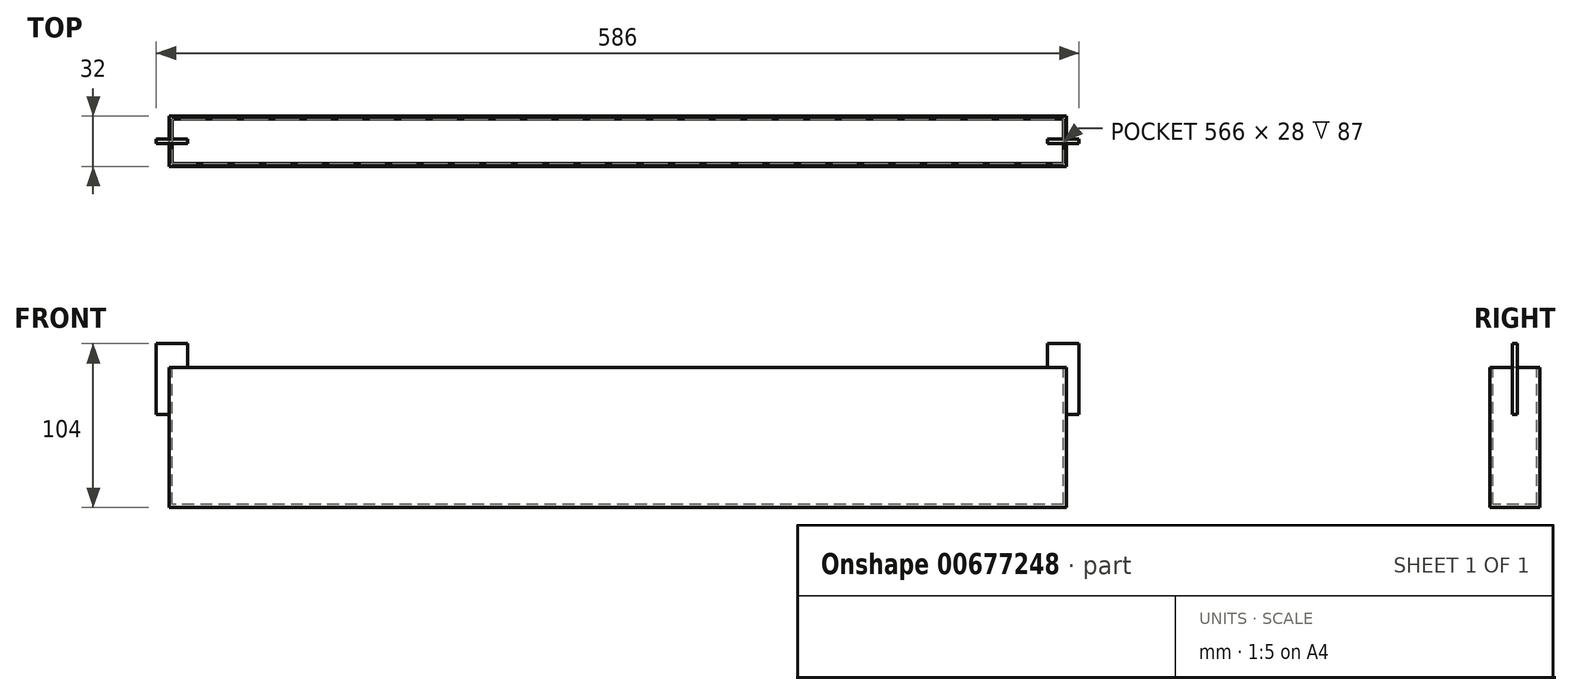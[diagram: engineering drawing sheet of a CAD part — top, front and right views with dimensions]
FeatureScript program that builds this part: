
annotation { "Feature Type Name" : "Feature", "Feature Type Description" : "" }
export const myFeature = defineFeature(function(context is Context, id is Id, definition is map)
    precondition{}
    {
        {
            var Q0;
            Q0=qCreatedBy(makeId("Top.planeOp"),FACE);
            var sketch = newSketch(context, id + "F0", { "sketchPlane" : qUnion([Q0])});
            skLineSegment(sketch, "E0.bottom", {"start": v(285, 16) * mm, "end": v(-285, 16) * mm});
            skLineSegment(sketch, "E0.top", {"start": v(285, -16) * mm, "end": v(-285, -16) * mm});
            skLineSegment(sketch, "E0.left", {"start": v(285, 16) * mm, "end": v(285, -16) * mm});
            skLineSegment(sketch, "E0.right", {"start": v(-285, 16) * mm, "end": v(-285, -16) * mm});
            skPoint(sketch, "E0.middle", {"position": v(0, 0) * mm});
            skSolve(sketch);
        }
        {
            var Q0;
            Q0=makeQuery(id+"F0.imprint","IMPRINT",FACE,{"disambiguationData":[TD([[makeQuery(id+"F0.imprint","IMPRINT",EDGE,{"derivedFrom":sQuery(id+"F0.wireOp",EDGE,"E0.bottom")}),1.0]])]});
            extrude(context, id + "F1", {"entities" : qUnion([Q0]), "depth" : 89 * mm, "offsetDistance" : 25 * mm});
        }
        {
            var Q0;
            Q0=makeQuery(id+"F1.opExtrude","SWEPT_FACE",FACE,{"disambiguationData":[OSD([sQuery(id+"F0.wireOp",EDGE,"E0.right")])]});
            var sketch = newSketch(context, id + "F2", { "sketchPlane" : qUnion([Q0])});
            skLineSegment(sketch, "E1.bottom", {"start": v(1.5, 89) * mm, "end": v(-1.5, 89) * mm});
            skLineSegment(sketch, "E1.top", {"start": v(1.5, 59) * mm, "end": v(-1.5, 59) * mm});
            skLineSegment(sketch, "E1.left", {"start": v(1.5, 89) * mm, "end": v(1.5, 59) * mm});
            skLineSegment(sketch, "E1.right", {"start": v(-1.5, 89) * mm, "end": v(-1.5, 59) * mm});
            skPoint(sketch, "E1.middle", {"position": v(0, 74) * mm});
            skSolve(sketch);
        }
        {
            var Q0;
            Q0=makeQuery(id+"F2.imprint","IMPRINT",FACE,{"disambiguationData":[TD([[makeQuery(id+"F2.imprint","IMPRINT",EDGE,{"derivedFrom":sQuery(id+"F2.wireOp",EDGE,"E1.bottom")}),-1.0]])]});
            extrude(context, id + "F3", {"entities" : qUnion([Q0]), "operationType" : NewBodyOperationType.ADD, "depth" : 8 * mm, "offsetDistance" : 25 * mm});
        }
        {
            var Q0;
            Q0=makeQuery(id+"F3.boolean.opBoolean","MERGE",FACE,{"derivedFrom":[makeQuery(id+"F1.opExtrude","CAP_FACE",FACE,{"disambiguationData":[OSD([sQuery(id+"F0.wireOp",EDGE,"E0.bottom"),sQuery(id+"F0.wireOp",EDGE,"E0.top"),sQuery(id+"F0.wireOp",EDGE,"E0.left"),sQuery(id+"F0.wireOp",EDGE,"E0.right")])],"isStart":false}),makeQuery(id+"F3.opExtrude","SWEPT_FACE",FACE,{"disambiguationData":[OSD([sQuery(id+"F2.wireOp",EDGE,"E1.bottom")])]})]});
            var sketch = newSketch(context, id + "F4", { "sketchPlane" : qUnion([Q0])});
            skLineSegment(sketch, "E2.bottom", {"start": v(-293, 1.5) * mm, "end": v(-285, 1.5) * mm});
            skLineSegment(sketch, "E2.top", {"start": v(-293, -1.5) * mm, "end": v(-285, -1.5) * mm});
            skLineSegment(sketch, "E2.left", {"start": v(-293, 1.5) * mm, "end": v(-293, -1.5) * mm});
            skLineSegment(sketch, "E2.right", {"start": v(-285, 1.5) * mm, "end": v(-285, -1.5) * mm});
            skSolve(sketch);
        }
        {
            var Q0;
            Q0=makeQuery(id+"F4.imprint","IMPRINT",FACE,{"disambiguationData":[TD([[makeQuery(id+"F4.imprint","IMPRINT",EDGE,{"derivedFrom":sQuery(id+"F4.wireOp",EDGE,"E2.bottom")}),-1.0]])]});
            extrude(context, id + "F5", {"entities" : qUnion([Q0]), "operationType" : NewBodyOperationType.ADD, "depth" : 15 * mm, "offsetDistance" : 25 * mm});
        }
        {
            var Q0;
            Q0=makeQuery(id+"F3.boolean.opBoolean","MERGE",FACE,{"derivedFrom":[makeQuery(id+"F1.opExtrude","CAP_FACE",FACE,{"disambiguationData":[OSD([sQuery(id+"F0.wireOp",EDGE,"E0.bottom"),sQuery(id+"F0.wireOp",EDGE,"E0.top"),sQuery(id+"F0.wireOp",EDGE,"E0.left"),sQuery(id+"F0.wireOp",EDGE,"E0.right")])],"isStart":false}),makeQuery(id+"F3.opExtrude","SWEPT_FACE",FACE,{"disambiguationData":[OSD([sQuery(id+"F2.wireOp",EDGE,"E1.bottom")])]})]});
            var sketch = newSketch(context, id + "F6", { "sketchPlane" : qUnion([Q0])});
            skLineSegment(sketch, "E3.bottom", {"start": v(283, 14) * mm, "end": v(-283, 14) * mm});
            skLineSegment(sketch, "E3.top", {"start": v(283, -14) * mm, "end": v(-283, -14) * mm});
            skLineSegment(sketch, "E3.left", {"start": v(283, 14) * mm, "end": v(283, -14) * mm});
            skLineSegment(sketch, "E3.right", {"start": v(-283, 14) * mm, "end": v(-283, -14) * mm});
            skPoint(sketch, "E3.middle", {"position": v(0, 0) * mm});
            skSolve(sketch);
        }
        {
            var Q0;
            {var subQ1=sQuery(id+"F6.wireOp",EDGE,"E3.bottom");Q0=makeQuery(id+"F6.imprint","IMPRINT",FACE,{"disambiguationData":[TD([[makeQuery(id+"F6.imprint","IMPRINT",EDGE,{"derivedFrom":subQ1}),1.0]])]});}
            extrude(context, id + "F7", {"entities" : qUnion([Q0]), "operationType" : NewBodyOperationType.REMOVE, "oppositeDirection" : true, "depth" : 87 * mm, "offsetDistance" : 25 * mm});
        }
        {
            var Q0;
            Q0=makeQuery(id+"F5.opExtrude","SWEPT_FACE",FACE,{"disambiguationData":[OSD([sQuery(id+"F4.wireOp",EDGE,"E2.right")])]});
            var sketch = newSketch(context, id + "F8", { "sketchPlane" : qUnion([Q0])});
            skLineSegment(sketch, "E4.bottom", {"start": v(-1.5, 104) * mm, "end": v(1.5, 104) * mm});
            skLineSegment(sketch, "E4.top", {"start": v(-1.5, 89) * mm, "end": v(1.5, 89) * mm});
            skLineSegment(sketch, "E4.left", {"start": v(-1.5, 104) * mm, "end": v(-1.5, 89) * mm});
            skLineSegment(sketch, "E4.right", {"start": v(1.5, 104) * mm, "end": v(1.5, 89) * mm});
            skSolve(sketch);
        }
        {
            var Q0;
            Q0=makeQuery(id+"F8.imprint","IMPRINT",FACE,{"disambiguationData":[TD([[makeQuery(id+"F8.imprint","IMPRINT",EDGE,{"derivedFrom":sQuery(id+"F8.wireOp",EDGE,"E4.bottom")}),1.0]])]});
            extrude(context, id + "F9", {"entities" : qUnion([Q0]), "operationType" : NewBodyOperationType.ADD, "depth" : 12 * mm, "offsetDistance" : 25 * mm});
        }
        {
            var Q0;
            Q0=makeQuery(id+"F1.opExtrude","SWEPT_FACE",FACE,{"disambiguationData":[OSD([sQuery(id+"F0.wireOp",EDGE,"E0.left")])]});
            var sketch = newSketch(context, id + "F10", { "sketchPlane" : qUnion([Q0])});
            skLineSegment(sketch, "E5.bottom", {"start": v(1.5, 89) * mm, "end": v(-1.5, 89) * mm});
            skLineSegment(sketch, "E5.top", {"start": v(1.5, 59) * mm, "end": v(-1.5, 59) * mm});
            skLineSegment(sketch, "E5.left", {"start": v(1.5, 89) * mm, "end": v(1.5, 59) * mm});
            skLineSegment(sketch, "E5.right", {"start": v(-1.5, 89) * mm, "end": v(-1.5, 59) * mm});
            skPoint(sketch, "E5.middle", {"position": v(0, 74) * mm});
            skLineSegment(sketch, "E6.top", {"start": v(1.5, 104) * mm, "end": v(-1.5, 104) * mm});
            skLineSegment(sketch, "E6.left", {"start": v(1.5, 89) * mm, "end": v(1.5, 104) * mm});
            skLineSegment(sketch, "E6.right", {"start": v(-1.5, 89) * mm, "end": v(-1.5, 104) * mm});
            skSolve(sketch);
        }
        {
            var Q0;
            Q0=makeQuery(id+"F10.imprint","IMPRINT",FACE,{"disambiguationData":[TD([[makeQuery(id+"F10.imprint","IMPRINT",EDGE,{"derivedFrom":sQuery(id+"F10.wireOp",EDGE,"E5.top")}),-1.0]])]});
            var Q1;
            Q1=makeQuery(id+"F10.imprint","IMPRINT",FACE,{"disambiguationData":[TD([[makeQuery(id+"F10.imprint","IMPRINT",EDGE,{"derivedFrom":sQuery(id+"F10.wireOp",EDGE,"E5.bottom")}),-1.0]])]});
            extrude(context, id + "F11", {"entities" : qUnion([Q0, Q1]), "operationType" : NewBodyOperationType.ADD, "depth" : 8 * mm, "offsetDistance" : 25 * mm});
        }
        {
            var Q0;
            Q0=makeQuery(id+"F11.opExtrude","CAP_FACE",FACE,{"disambiguationData":[OSD([sQuery(id+"F10.wireOp",EDGE,"E5.top"),sQuery(id+"F10.wireOp",EDGE,"E5.left"),sQuery(id+"F10.wireOp",EDGE,"E5.right"),sQuery(id+"F10.wireOp",EDGE,"E6.top"),sQuery(id+"F10.wireOp",EDGE,"E6.left"),sQuery(id+"F10.wireOp",EDGE,"E6.right")])],"isStart":true});
            var sketch = newSketch(context, id + "F12", { "sketchPlane" : qUnion([Q0])});
            skLineSegment(sketch, "E7.bottom", {"start": v(1.5, 104) * mm, "end": v(-1.5, 104) * mm});
            skLineSegment(sketch, "E7.top", {"start": v(1.5, 89) * mm, "end": v(-1.5, 89) * mm});
            skLineSegment(sketch, "E7.left", {"start": v(1.5, 104) * mm, "end": v(1.5, 89) * mm});
            skLineSegment(sketch, "E7.right", {"start": v(-1.5, 104) * mm, "end": v(-1.5, 89) * mm});
            skSolve(sketch);
        }
        {
            var Q0;
            Q0=makeQuery(id+"F12.imprint","IMPRINT",FACE,{"disambiguationData":[TD([[makeQuery(id+"F12.imprint","IMPRINT",EDGE,{"derivedFrom":sQuery(id+"F12.wireOp",EDGE,"E7.bottom")}),-1.0]])]});
            extrude(context, id + "F13", {"entities" : qUnion([Q0]), "operationType" : NewBodyOperationType.ADD, "depth" : 12 * mm, "offsetDistance" : 25 * mm});
        }
    });
